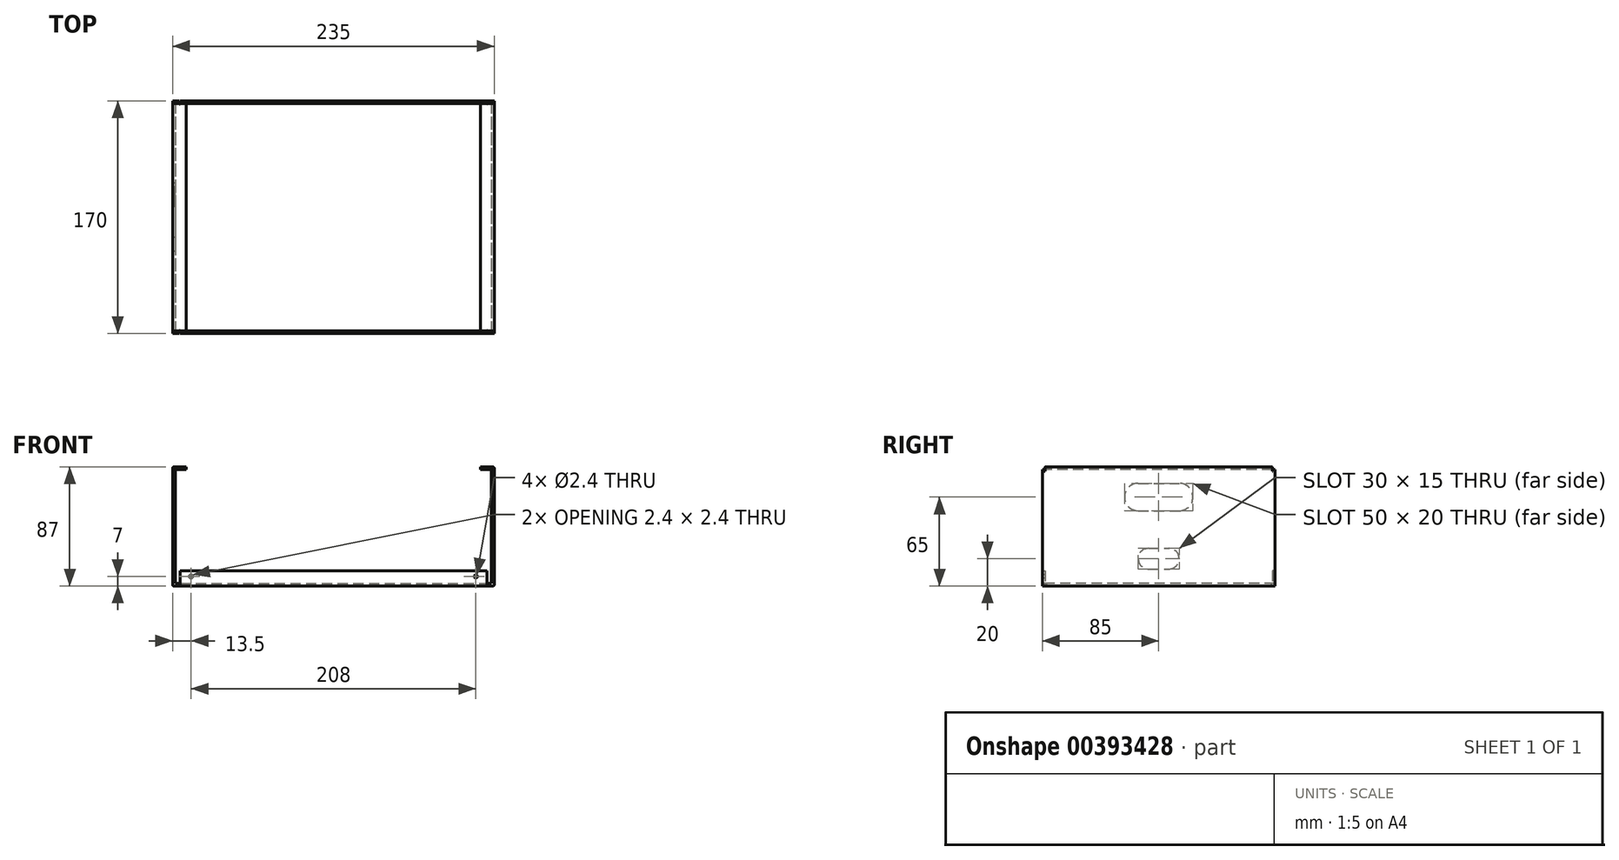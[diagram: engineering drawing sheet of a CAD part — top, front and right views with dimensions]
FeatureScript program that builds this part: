
annotation { "Feature Type Name" : "Feature", "Feature Type Description" : "" }
export const myFeature = defineFeature(function(context is Context, id is Id, definition is map)
    precondition{}
    {
        {
            var Q0;
            Q0=qCreatedBy(makeId("Top.planeOp"),FACE);
            var sketch = newSketch(context, id + "F0", { "sketchPlane" : qUnion([Q0])});
            skLineSegment(sketch, "E0.bottom", {"start": v(117.5, -85) * mm, "end": v(112.5, -85) * mm});
            skLineSegment(sketch, "E0.top", {"start": v(117.5, 85) * mm, "end": v(112.5, 85) * mm});
            skLineSegment(sketch, "E0.left", {"start": v(117.5, -85) * mm, "end": v(117.5, 85) * mm});
            skLineSegment(sketch, "E0.right", {"start": v(-117.5, -85) * mm, "end": v(-117.5, 85) * mm});
            skPoint(sketch, "E0.middle", {"position": v(0, 0) * mm});
            skLineSegment(sketch, "E1.top", {"start": v(-112.5, -82) * mm, "end": v(-112, -82) * mm});
            skLineSegment(sketch, "E1.left", {"start": v(-112.5, -85) * mm, "end": v(-112.5, -82) * mm});
            skLineSegment(sketch, "E1.right", {"start": v(-112, -85) * mm, "end": v(-112, -82) * mm});
            skLineSegment(sketch, "E2.trimOffspring", {"start": v(-112.5, -85) * mm, "end": v(-117.5, -85) * mm});
            skLineSegment(sketch, "E3.top", {"start": v(112, -82) * mm, "end": v(112.5, -82) * mm});
            skLineSegment(sketch, "E3.left", {"start": v(112, -85) * mm, "end": v(112, -82) * mm});
            skLineSegment(sketch, "E3.right", {"start": v(112.5, -85) * mm, "end": v(112.5, -82) * mm});
            skLineSegment(sketch, "E4.trimOffspring", {"start": v(112, -85) * mm, "end": v(-112, -85) * mm});
            skLineSegment(sketch, "E5.top", {"start": v(-112.5, 82) * mm, "end": v(-112, 82) * mm});
            skLineSegment(sketch, "E5.left", {"start": v(-112.5, 85) * mm, "end": v(-112.5, 82) * mm});
            skLineSegment(sketch, "E5.right", {"start": v(-112, 85) * mm, "end": v(-112, 82) * mm});
            skLineSegment(sketch, "E6.top", {"start": v(112.5, 82) * mm, "end": v(112, 82) * mm});
            skLineSegment(sketch, "E6.left", {"start": v(112.5, 85) * mm, "end": v(112.5, 82) * mm});
            skLineSegment(sketch, "E6.right", {"start": v(112, 85) * mm, "end": v(112, 82) * mm});
            skLineSegment(sketch, "E7.trimOffspring", {"start": v(-112.5, 85) * mm, "end": v(-117.5, 85) * mm});
            skLineSegment(sketch, "E8.trimOffspring", {"start": v(112, 85) * mm, "end": v(-112, 85) * mm});
            skSolve(sketch);
        }
        {
            var Q0;
            Q0=qSketchRegion(id+"F0",true);
            extrude(context, id + "F1", {"entities" : qUnion([Q0]), "depth" : 2 * mm});
        }
        {
            var Q0;
            Q0=makeQuery(id+"F1.opExtrude","CAP_FACE",FACE,{"disambiguationData":[OSD([sQuery(id+"F0.wireOp",EDGE,"E0.bottom"),sQuery(id+"F0.wireOp",EDGE,"E0.top"),sQuery(id+"F0.wireOp",EDGE,"E0.left"),sQuery(id+"F0.wireOp",EDGE,"E0.right")])],"isStart":false});
            var sketch = newSketch(context, id + "F2", { "sketchPlane" : qUnion([Q0])});
            skLineSegment(sketch, "E9.bottom", {"start": v(117.5, 85) * mm, "end": v(115.5, 85) * mm});
            skLineSegment(sketch, "E9.top", {"start": v(117.5, -85) * mm, "end": v(115.5, -85) * mm});
            skLineSegment(sketch, "E9.left", {"start": v(117.5, 85) * mm, "end": v(117.5, -85) * mm});
            skLineSegment(sketch, "E9.right", {"start": v(115.5, 85) * mm, "end": v(115.5, -85) * mm});
            skLineSegment(sketch, "E10.bottom", {"start": v(-117.5, 85) * mm, "end": v(-115.5, 85) * mm});
            skLineSegment(sketch, "E10.top", {"start": v(-117.5, -85) * mm, "end": v(-115.5, -85) * mm});
            skLineSegment(sketch, "E10.left", {"start": v(-117.5, 85) * mm, "end": v(-117.5, -85) * mm});
            skLineSegment(sketch, "E10.right", {"start": v(-115.5, 85) * mm, "end": v(-115.5, -85) * mm});
            skSolve(sketch);
        }
        {
            var Q0;
            Q0=qSketchRegion(id+"F2",true);
            extrude(context, id + "F3", {"entities" : qUnion([Q0]), "operationType" : NewBodyOperationType.ADD, "depth" : 83 * mm});
        }
        {
            var Q0;
            Q0=makeQuery(id+"F1.opExtrude","CAP_EDGE",EDGE,{"disambiguationData":[OSD([sQuery(id+"F0.wireOp",EDGE,"E0.right")])],"isStart":true});
            var Q1;
            Q1=makeQuery(id+"F1.opExtrude","CAP_EDGE",EDGE,{"disambiguationData":[OSD([sQuery(id+"F0.wireOp",EDGE,"E0.left")])],"isStart":true});
            var Q2;
            Q2=makeQuery(id+"F3.opExtrude","CAP_EDGE",EDGE,{"disambiguationData":[OSD([sQuery(id+"F2.wireOp",EDGE,"E10.right")])],"isStart":true});
            var Q3;
            Q3=makeQuery(id+"F3.opExtrude","CAP_EDGE",EDGE,{"disambiguationData":[OSD([sQuery(id+"F2.wireOp",EDGE,"E9.right")])],"isStart":true});
            fillet(context, id + "F4", {"entities" : qUnion([Q0, Q1, Q2, Q3]), "radius" : 1 * mm, "tangentPropagation" : true, "allowEdgeOverflow" : false});
        }
        {
            var Q0;
            Q0=makeQuery(id+"F3.opExtrude","CAP_FACE",FACE,{"disambiguationData":[OSD([sQuery(id+"F2.wireOp",EDGE,"E10.bottom"),sQuery(id+"F2.wireOp",EDGE,"E10.top"),sQuery(id+"F2.wireOp",EDGE,"E10.left"),sQuery(id+"F2.wireOp",EDGE,"E10.right")])],"isStart":false});
            var sketch = newSketch(context, id + "F5", { "sketchPlane" : qUnion([Q0])});
            skLineSegment(sketch, "E11.bottom", {"start": v(-117.5, 83) * mm, "end": v(-107.5, 83) * mm});
            skLineSegment(sketch, "E11.top", {"start": v(-117.5, -83) * mm, "end": v(-107.5, -83) * mm});
            skLineSegment(sketch, "E11.left", {"start": v(-117.5, 83) * mm, "end": v(-117.5, -83) * mm});
            skLineSegment(sketch, "E11.right", {"start": v(-107.5, 83) * mm, "end": v(-107.5, -83) * mm});
            skLineSegment(sketch, "E12.bottom", {"start": v(107.5, 83) * mm, "end": v(117.5, 83) * mm});
            skLineSegment(sketch, "E12.top", {"start": v(107.5, -83) * mm, "end": v(117.5, -83) * mm});
            skLineSegment(sketch, "E12.left", {"start": v(107.5, 83) * mm, "end": v(107.5, -83) * mm});
            skLineSegment(sketch, "E12.right", {"start": v(117.5, 83) * mm, "end": v(117.5, -83) * mm});
            skSolve(sketch);
        }
        {
            var Q0;
            Q0=qSketchRegion(id+"F5",true);
            extrude(context, id + "F6", {"entities" : qUnion([Q0]), "operationType" : NewBodyOperationType.ADD, "depth" : 2 * mm});
        }
        {
            var Q0;
            Q0=makeQuery(id+"F6.opExtrude","CAP_EDGE",EDGE,{"disambiguationData":[OSD([sQuery(id+"F5.wireOp",EDGE,"E11.left")])],"isStart":false});
            var Q1;
            Q1=makeQuery(id+"F6.opExtrude","CAP_EDGE",EDGE,{"disambiguationData":[OSD([sQuery(id+"F5.wireOp",EDGE,"E12.right")])],"isStart":false});
            var Q2;
            {var subQ0=sQuery(id+"F5.wireOp",EDGE,"E11.top");var subQ1=sQuery(id+"F5.wireOp",EDGE,"E11.bottom");var subQ2=sQuery(id+"F2.wireOp",EDGE,"E10.right");Q2=makeQuery(id+"F6.boolean.opBoolean","SPLIT",EDGE,{"disambiguationData":[TD([makeQuery(id+"F3.opExtrude","CAP_FACE",FACE,{"disambiguationData":[OSD([sQuery(id+"F2.wireOp",EDGE,"E10.bottom"),sQuery(id+"F2.wireOp",EDGE,"E10.top"),sQuery(id+"F2.wireOp",EDGE,"E10.left"),subQ2])],"isStart":false}),makeQuery(id+"F3.opExtrude","SWEPT_FACE",FACE,{"disambiguationData":[OSD([subQ2])]}),makeQuery(id+"F6.opExtrude","SWEPT_FACE",FACE,{"disambiguationData":[OSD([subQ1])]}),makeQuery(id+"F6.opExtrude","CAP_FACE",FACE,{"disambiguationData":[OSD([subQ1,subQ0,sQuery(id+"F5.wireOp",EDGE,"E11.left"),sQuery(id+"F5.wireOp",EDGE,"E11.right")])],"isStart":true}),makeQuery(id+"F6.opExtrude","SWEPT_FACE",FACE,{"disambiguationData":[OSD([subQ0])]})])],"derivedFrom":makeQuery(id+"F3.opExtrude","CAP_EDGE",EDGE,{"disambiguationData":[OSD([subQ2])],"isStart":false})});}
            var Q3;
            {var subQ0=sQuery(id+"F5.wireOp",EDGE,"E12.top");var subQ1=sQuery(id+"F5.wireOp",EDGE,"E12.bottom");var subQ2=sQuery(id+"F2.wireOp",EDGE,"E9.right");Q3=makeQuery(id+"F6.boolean.opBoolean","SPLIT",EDGE,{"disambiguationData":[TD([makeQuery(id+"F3.opExtrude","CAP_FACE",FACE,{"disambiguationData":[OSD([sQuery(id+"F2.wireOp",EDGE,"E9.bottom"),sQuery(id+"F2.wireOp",EDGE,"E9.top"),sQuery(id+"F2.wireOp",EDGE,"E9.left"),subQ2])],"isStart":false}),makeQuery(id+"F3.opExtrude","SWEPT_FACE",FACE,{"disambiguationData":[OSD([subQ2])]}),makeQuery(id+"F6.opExtrude","SWEPT_FACE",FACE,{"disambiguationData":[OSD([subQ1])]}),makeQuery(id+"F6.opExtrude","CAP_FACE",FACE,{"disambiguationData":[OSD([subQ1,subQ0,sQuery(id+"F5.wireOp",EDGE,"E12.left"),sQuery(id+"F5.wireOp",EDGE,"E12.right")])],"isStart":true}),makeQuery(id+"F6.opExtrude","SWEPT_FACE",FACE,{"disambiguationData":[OSD([subQ0])]})])],"derivedFrom":makeQuery(id+"F3.opExtrude","CAP_EDGE",EDGE,{"disambiguationData":[OSD([subQ2])],"isStart":false})});}
            fillet(context, id + "F7", {"entities" : qUnion([Q0, Q1, Q2, Q3]), "radius" : 1 * mm, "tangentPropagation" : true, "allowEdgeOverflow" : false});
        }
        {
            var Q0;
            Q0=makeQuery(id+"F1.opExtrude","CAP_FACE",FACE,{"disambiguationData":[OSD([sQuery(id+"F0.wireOp",EDGE,"E0.bottom"),sQuery(id+"F0.wireOp",EDGE,"E0.top"),sQuery(id+"F0.wireOp",EDGE,"E0.left"),sQuery(id+"F0.wireOp",EDGE,"E0.right"),sQuery(id+"F0.wireOp",EDGE,"E1.top"),sQuery(id+"F0.wireOp",EDGE,"E1.left"),sQuery(id+"F0.wireOp",EDGE,"E1.right"),sQuery(id+"F0.wireOp",EDGE,"E2.trimOffspring"),sQuery(id+"F0.wireOp",EDGE,"E3.top"),sQuery(id+"F0.wireOp",EDGE,"E3.left"),sQuery(id+"F0.wireOp",EDGE,"E3.right"),sQuery(id+"F0.wireOp",EDGE,"E4.trimOffspring")])],"isStart":false});
            var sketch = newSketch(context, id + "F8", { "sketchPlane" : qUnion([Q0])});
            skLineSegment(sketch, "E13.bottom", {"start": v(-112, -83) * mm, "end": v(112, -83) * mm});
            skLineSegment(sketch, "E13.top", {"start": v(-112, -85) * mm, "end": v(112, -85) * mm});
            skLineSegment(sketch, "E13.left", {"start": v(-112, -83) * mm, "end": v(-112, -85) * mm});
            skLineSegment(sketch, "E13.right", {"start": v(112, -83) * mm, "end": v(112, -85) * mm});
            skLineSegment(sketch, "E14.bottom", {"start": v(-112, 85) * mm, "end": v(112, 85) * mm});
            skLineSegment(sketch, "E14.top", {"start": v(-112, 83) * mm, "end": v(112, 83) * mm});
            skLineSegment(sketch, "E14.left", {"start": v(-112, 85) * mm, "end": v(-112, 83) * mm});
            skLineSegment(sketch, "E14.right", {"start": v(112, 85) * mm, "end": v(112, 83) * mm});
            skSolve(sketch);
        }
        {
            var Q0;
            Q0=qSketchRegion(id+"F8",true);
            extrude(context, id + "F9", {"entities" : qUnion([Q0]), "operationType" : NewBodyOperationType.ADD, "depth" : 9 * mm});
        }
        {
            var Q0;
            Q0=makeQuery(id+"F1.opExtrude","CAP_EDGE",EDGE,{"disambiguationData":[OSD([sQuery(id+"F0.wireOp",EDGE,"E4.trimOffspring")])],"isStart":true});
            var Q1;
            Q1=makeQuery(id+"F9.opExtrude","CAP_EDGE",EDGE,{"disambiguationData":[OSD([sQuery(id+"F8.wireOp",EDGE,"E13.bottom")])],"isStart":true});
            var Q2;
            Q2=makeQuery(id+"F9.opExtrude","CAP_EDGE",EDGE,{"disambiguationData":[OSD([sQuery(id+"F8.wireOp",EDGE,"E14.top")])],"isStart":true});
            var Q3;
            Q3=makeQuery(id+"F1.opExtrude","CAP_EDGE",EDGE,{"disambiguationData":[OSD([sQuery(id+"F0.wireOp",EDGE,"E8.trimOffspring")])],"isStart":true});
            fillet(context, id + "F10", {"entities" : qUnion([Q0, Q1, Q2, Q3]), "radius" : 1 * mm, "tangentPropagation" : true, "allowEdgeOverflow" : false});
        }
        {
            var Q0;
            Q0=makeQuery(id+"F6.boolean.opBoolean","MERGE",FACE,{"derivedFrom":[makeQuery(id+"F3.boolean.opBoolean","MERGE",FACE,{"derivedFrom":[makeQuery(id+"F1.opExtrude","SWEPT_FACE",FACE,{"disambiguationData":[OSD([sQuery(id+"F0.wireOp",EDGE,"E0.right")])]}),makeQuery(id+"F3.opExtrude","SWEPT_FACE",FACE,{"disambiguationData":[OSD([sQuery(id+"F2.wireOp",EDGE,"LtGDmYED-3yVl-KpR6-pZyB-YukeFVbaKuZ8.left")])]})]}),makeQuery(id+"F6.opExtrude","SWEPT_FACE",FACE,{"disambiguationData":[OSD([sQuery(id+"F5.wireOp",EDGE,"E11.left")])]})]});
            var sketch = newSketch(context, id + "F11", { "sketchPlane" : qUnion([Q0])});
            skLineSegment(sketch, "E15.bottom", {"start": v(83, 85) * mm, "end": v(83.5, 85) * mm});
            skLineSegment(sketch, "E15.top", {"start": v(83, 84) * mm, "end": v(83.5, 84) * mm});
            skLineSegment(sketch, "E15.left", {"start": v(83, 85) * mm, "end": v(83, 84) * mm});
            skLineSegment(sketch, "E15.right", {"start": v(83.5, 85) * mm, "end": v(83.5, 84) * mm});
            skLineSegment(sketch, "E16.bottom", {"start": v(-83, 85) * mm, "end": v(-83.5, 85) * mm});
            skLineSegment(sketch, "E16.top", {"start": v(-83, 84) * mm, "end": v(-83.5, 84) * mm});
            skLineSegment(sketch, "E16.left", {"start": v(-83, 85) * mm, "end": v(-83, 84) * mm});
            skLineSegment(sketch, "E16.right", {"start": v(-83.5, 85) * mm, "end": v(-83.5, 84) * mm});
            skSolve(sketch);
        }
        {
            var Q0;
            Q0=qSketchRegion(id+"F11",true);
            extrude(context, id + "F12", {"entities" : qUnion([Q0]), "operationType" : NewBodyOperationType.REMOVE, "endBound" : BoundingType.THROUGH_ALL, "oppositeDirection" : true, "depth" : 25 * mm});
        }
        {
            var Q0;
            Q0=makeQuery(id+"F6.boolean.opBoolean","MERGE",FACE,{"derivedFrom":[makeQuery(id+"F3.boolean.opBoolean","MERGE",FACE,{"derivedFrom":[makeQuery(id+"F1.opExtrude","SWEPT_FACE",FACE,{"disambiguationData":[OSD([sQuery(id+"F0.wireOp",EDGE,"E0.right")])]}),makeQuery(id+"F3.opExtrude","SWEPT_FACE",FACE,{"disambiguationData":[OSD([sQuery(id+"F2.wireOp",EDGE,"E10.left")])]})]}),makeQuery(id+"F6.opExtrude","SWEPT_FACE",FACE,{"disambiguationData":[OSD([sQuery(id+"F5.wireOp",EDGE,"E11.left")])]})]});
            var sketch = newSketch(context, id + "F13", { "sketchPlane" : qUnion([Q0])});
            skCircle(sketch, "E17", {"center": v(0, 20) * mm, "radius": 7.5 * mm, "construction": true});
            skLineSegment(sketch, "E18.bottom", {"start": v(7.5, 12.5) * mm, "end": v(-7.5, 12.5) * mm});
            skLineSegment(sketch, "E18.top", {"start": v(7.5, 27.5) * mm, "end": v(-7.5, 27.5) * mm});
            skArc(sketch, "E19", {"start": v(-7.5, 27.5) * mm, "mid": v(-15, 20) * mm, "end": v(-7.5, 12.5) * mm});
            skArc(sketch, "E20", {"start": v(7.5, 27.5) * mm, "mid": v(15, 20) * mm, "end": v(7.5, 12.5) * mm});
            skLineSegment(sketch, "E21.bottom", {"start": v(15, 55) * mm, "end": v(-15, 55) * mm});
            skLineSegment(sketch, "E21.top", {"start": v(15, 75) * mm, "end": v(-15, 75) * mm});
            skArc(sketch, "E22", {"start": v(-15, 75) * mm, "mid": v(-25, 65) * mm, "end": v(-15, 55) * mm});
            skArc(sketch, "E23", {"start": v(15, 75) * mm, "mid": v(25, 65) * mm, "end": v(15, 55) * mm});
            skSolve(sketch);
        }
        {
            var Q0;
            Q0=qSketchRegion(id+"F13",true);
            extrude(context, id + "F14", {"entities" : qUnion([Q0]), "operationType" : NewBodyOperationType.REMOVE, "oppositeDirection" : true, "depth" : 3 * mm});
        }
        {
            var Q0;
            Q0=makeQuery(id+"F9.boolean.opBoolean","MERGE",FACE,{"derivedFrom":[makeQuery(id+"F1.opExtrude","SWEPT_FACE",FACE,{"disambiguationData":[OSD([sQuery(id+"F0.wireOp",EDGE,"E4.trimOffspring")])]}),makeQuery(id+"F9.opExtrude","SWEPT_FACE",FACE,{"disambiguationData":[OSD([sQuery(id+"F8.wireOp",EDGE,"E13.top")])]})]});
            var sketch = newSketch(context, id + "F15", { "sketchPlane" : qUnion([Q0])});
            skCircle(sketch, "E24", {"center": v(104, 7) * mm, "radius": 1.2 * mm});
            skCircle(sketch, "E25", {"center": v(-104, 7) * mm, "radius": 1.2 * mm});
            skSolve(sketch);
        }
        {
            var Q0;
            Q0=qSketchRegion(id+"F15",true);
            extrude(context, id + "F16", {"entities" : qUnion([Q0]), "operationType" : NewBodyOperationType.REMOVE, "endBound" : BoundingType.THROUGH_ALL, "oppositeDirection" : true, "depth" : 25 * mm});
        }
    });
